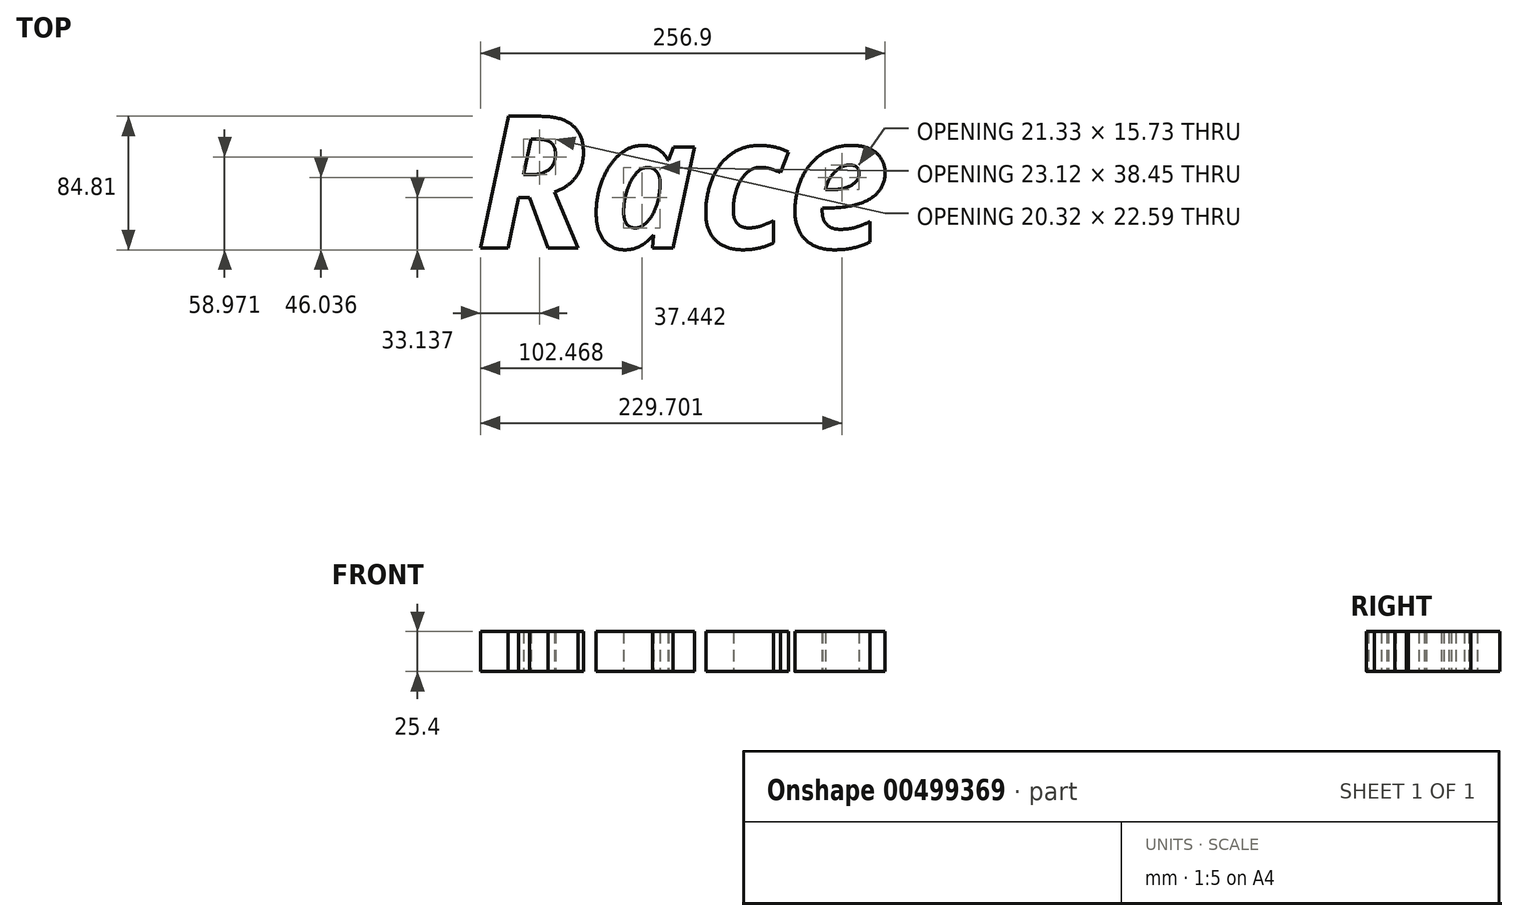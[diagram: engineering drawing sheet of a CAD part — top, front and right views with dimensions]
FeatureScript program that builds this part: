
annotation { "Feature Type Name" : "Feature", "Feature Type Description" : "" }
export const myFeature = defineFeature(function(context is Context, id is Id, definition is map)
    precondition{}
    {
        {
            var Q0;
            Q0=qCreatedBy(makeId("Top.planeOp"),FACE);
            var sketch = newSketch(context, id + "F0", { "sketchPlane" : qUnion([Q0])});
            skText(sketch, "E0", { "text": "Race", "fontName": "OpenSans-BoldItalic.ttf"});
            const initialGuessF0  = {"E0": [-0.124, -0.03489, 1, 0, 0.08437]};
            skSetInitialGuess(sketch, initialGuessF0);
            skSolve(sketch);
        }
        {
            var Q0;
            Q0 = qSketchRegion(id + "F0", true);
            extrude(context, id + "F1", {"entities" : qUnion([Q0]), "depth" : 25.4 * mm});
        }
    });
